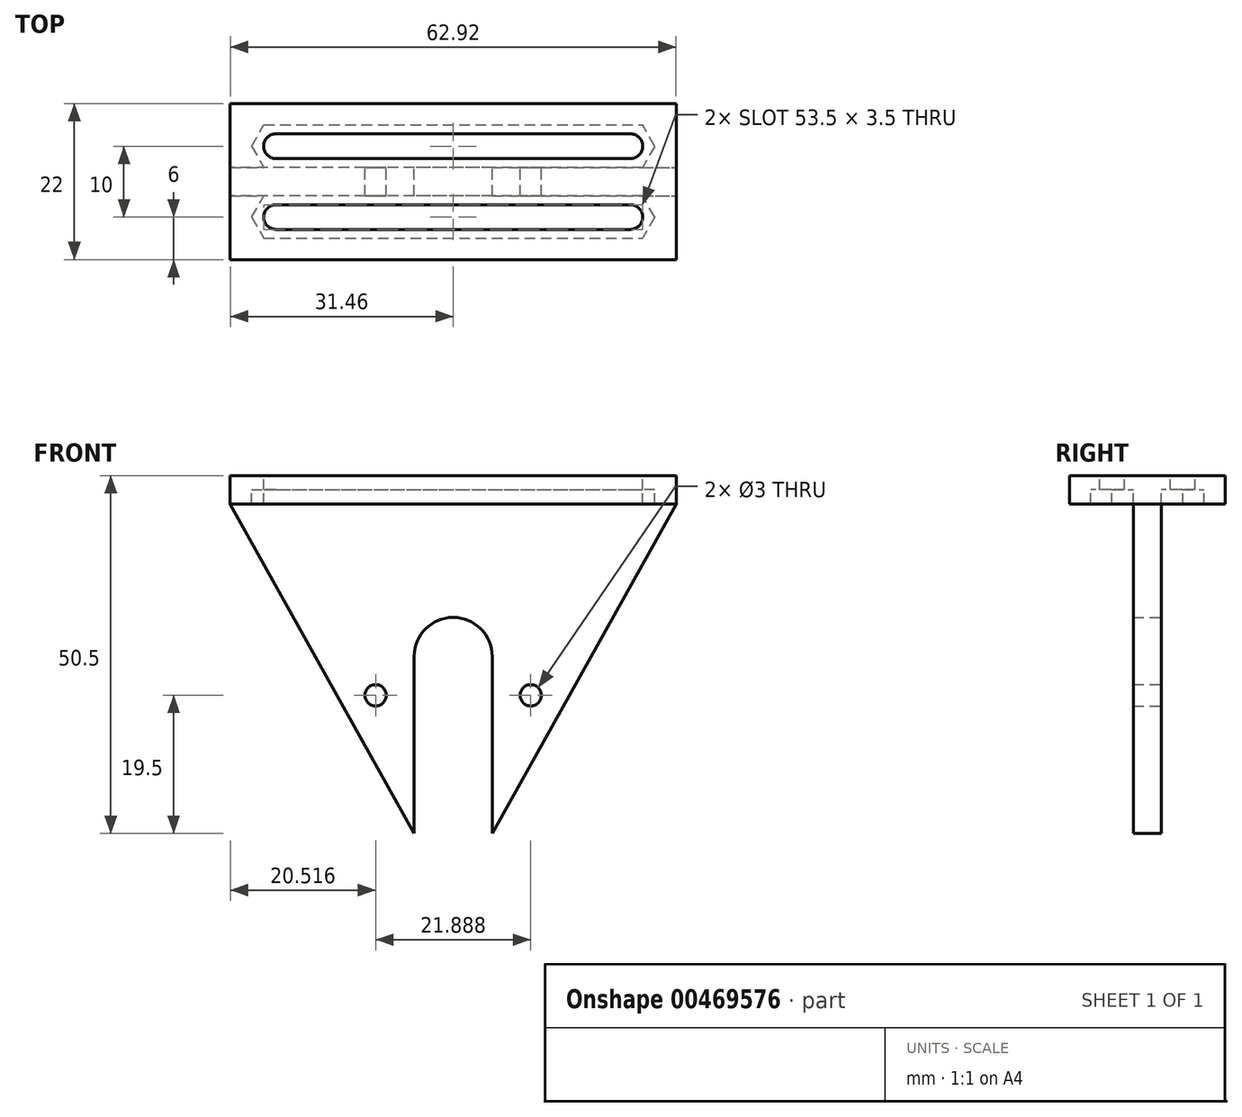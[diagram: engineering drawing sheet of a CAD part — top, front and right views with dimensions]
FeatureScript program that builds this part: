
annotation { "Feature Type Name" : "Feature", "Feature Type Description" : "" }
export const myFeature = defineFeature(function(context is Context, id is Id, definition is map)
    precondition{}
    {
        {
            var Q0;
            Q0=qCreatedBy(makeId("Top.planeOp"),FACE);
            var sketch = newSketch(context, id + "F0", { "sketchPlane" : qUnion([Q0])});
            skArc(sketch, "E0", {"start": v(-25, 6.75) * mm, "mid": v(-26.75, 5) * mm, "end": v(-25, 3.25) * mm});
            skArc(sketch, "E1.MirrorCS", {"start": v(25, 6.75) * mm, "mid": v(26.75, 5) * mm, "end": v(25, 3.25) * mm});
            skLineSegment(sketch, "E2", {"start": v(-25, 6.75) * mm, "end": v(25, 6.75) * mm});
            skLineSegment(sketch, "E3", {"start": v(-25, 3.25) * mm, "end": v(25, 3.25) * mm});
            skLineSegment(sketch, "E4.MirrorCS", {"start": v(-25, -3.25) * mm, "end": v(25, -3.25) * mm});
            skLineSegment(sketch, "E5.MirrorCS", {"start": v(-25, -6.75) * mm, "end": v(25, -6.75) * mm});
            skArc(sketch, "E6.MirrorCS", {"start": v(-25, -6.75) * mm, "mid": v(-26.75, -5) * mm, "end": v(-25, -3.25) * mm});
            skArc(sketch, "E7.MirrorCS", {"start": v(25, -6.75) * mm, "mid": v(26.75, -5) * mm, "end": v(25, -3.25) * mm});
            skLineSegment(sketch, "E8.bottom", {"start": v(31.46, 11) * mm, "end": v(-31.46, 11) * mm});
            skLineSegment(sketch, "E8.top", {"start": v(31.46, -11) * mm, "end": v(-31.46, -11) * mm});
            skLineSegment(sketch, "E8.left", {"start": v(31.46, 11) * mm, "end": v(31.46, -11) * mm});
            skLineSegment(sketch, "E8.right", {"start": v(-31.46, 11) * mm, "end": v(-31.46, -11) * mm});
            skPoint(sketch, "E8.middle", {"position": v(0, 0) * mm});
            skLineSegment(sketch, "E9", {"start": v(-28.46, 5) * mm, "end": v(-26.73, 8) * mm});
            skLineSegment(sketch, "E10", {"start": v(-25, 5) * mm, "end": v(25, 5) * mm, "construction": true});
            skLineSegment(sketch, "E11.MirrorCS", {"start": v(-28.46, 5) * mm, "end": v(-26.73, 2) * mm});
            skLineSegment(sketch, "E12.MirrorCS", {"start": v(28.46, 5) * mm, "end": v(26.73, 8) * mm});
            skLineSegment(sketch, "E13.MirrorCS", {"start": v(28.46, 5) * mm, "end": v(26.73, 2) * mm});
            skLineSegment(sketch, "E14", {"start": v(-26.73, 8) * mm, "end": v(26.73, 8) * mm});
            skLineSegment(sketch, "E15", {"start": v(26.73, 2) * mm, "end": v(-26.73, 2) * mm});
            skLineSegment(sketch, "E16.MirrorCS", {"start": v(26.73, -2) * mm, "end": v(-26.73, -2) * mm});
            skLineSegment(sketch, "E17.MirrorCS", {"start": v(-28.46, -5) * mm, "end": v(-26.73, -2) * mm});
            skLineSegment(sketch, "E18.MirrorCS", {"start": v(-28.46, -5) * mm, "end": v(-26.73, -8) * mm});
            skLineSegment(sketch, "E19.MirrorCS", {"start": v(-26.73, -8) * mm, "end": v(26.73, -8) * mm});
            skLineSegment(sketch, "E20.MirrorCS", {"start": v(28.46, -5) * mm, "end": v(26.73, -8) * mm});
            skLineSegment(sketch, "E21.MirrorCS", {"start": v(28.46, -5) * mm, "end": v(26.73, -2) * mm});
            skLineSegment(sketch, "E22", {"start": v(-27.6, 6.5) * mm, "end": v(-25, 5) * mm, "construction": true});
            skLineSegment(sketch, "E23", {"start": v(-27.6, 3.5) * mm, "end": v(-25, 5) * mm, "construction": true});
            skSolve(sketch);
        }
        {
            var Q0;
            Q0=makeQuery(id+"F0.imprint","IMPRINT",FACE,{"disambiguationData":[TD([[makeQuery(id+"F0.imprint","IMPRINT",EDGE,{"derivedFrom":sQuery(id+"F0.wireOp",EDGE,"E8.bottom")}),1.0]])]});
            extrude(context, id + "F1", {"entities" : qUnion([Q0]), "oppositeDirection" : true, "depth" : 4 * mm});
        }
        {
            var Q0;
            Q0=makeQuery(id+"F0.imprint","IMPRINT",FACE,{"disambiguationData":[TD([[makeQuery(id+"F0.imprint","IMPRINT",EDGE,{"derivedFrom":sQuery(id+"F0.wireOp",EDGE,"E4.MirrorCS")}),1.0]])]});
            var Q1;
            Q1=makeQuery(id+"F0.imprint","IMPRINT",FACE,{"disambiguationData":[TD([[makeQuery(id+"F0.imprint","IMPRINT",EDGE,{"derivedFrom":sQuery(id+"F0.wireOp",EDGE,"E0")}),-1.0]])]});
            extrude(context, id + "F2", {"entities" : qUnion([Q0, Q1]), "operationType" : NewBodyOperationType.ADD, "oppositeDirection" : true, "depth" : 2 * mm});
        }
        {
            var Q0;
            Q0=qCreatedBy(makeId("Front.planeOp"),FACE);
            var sketch = newSketch(context, id + "F3", { "sketchPlane" : qUnion([Q0])});
            skArc(sketch, "E24", {"start": v(-5.5, -25.5) * mm, "mid": v(0, -20) * mm, "end": v(5.5, -25.5) * mm});
            skArc(sketch, "E25", {"start": v(-5.5, -25.5) * mm, "mid": v(0, -31) * mm, "end": v(5.5, -25.5) * mm, "construction": true});
            skLineSegment(sketch, "E26", {"start": v(-5.5, -25.5) * mm, "end": v(-5.5, -50.5) * mm});
            skLineSegment(sketch, "E27", {"start": v(-5.5, -50.5) * mm, "end": v(-31.46, -4) * mm});
            skLineSegment(sketch, "E28.MirrorCS", {"start": v(5.5, -50.5) * mm, "end": v(31.46, -4) * mm});
            skLineSegment(sketch, "E29.MirrorCS", {"start": v(5.5, -25.5) * mm, "end": v(5.5, -50.5) * mm});
            skLineSegment(sketch, "E30", {"start": v(-31.46, -4) * mm, "end": v(31.46, -4) * mm});
            skPoint(sketch, "E31", {"position": v(0, -31) * mm});
            skLineSegment(sketch, "E32", {"start": v(-5.5, -31) * mm, "end": v(-16.39, -31) * mm, "construction": true});
            skCircle(sketch, "E33", {"center": v(-10.94, -31) * mm, "radius": 1.5 * mm});
            skLineSegment(sketch, "E34.MirrorCS", {"start": v(5.5, -31) * mm, "end": v(16.39, -31) * mm, "construction": true});
            skCircle(sketch, "E35.MirrorC", {"center": v(10.94, -31) * mm, "radius": 1.5 * mm});
            skSolve(sketch);
        }
        {
            var Q0;
            Q0 = qSketchRegion(id + "F3", true);
            extrude(context, id + "F4", {"entities" : qUnion([Q0]), "operationType" : NewBodyOperationType.ADD, "endBound" : BoundingType.SYMMETRIC, "depth" : 4 * mm});
        }
    });
